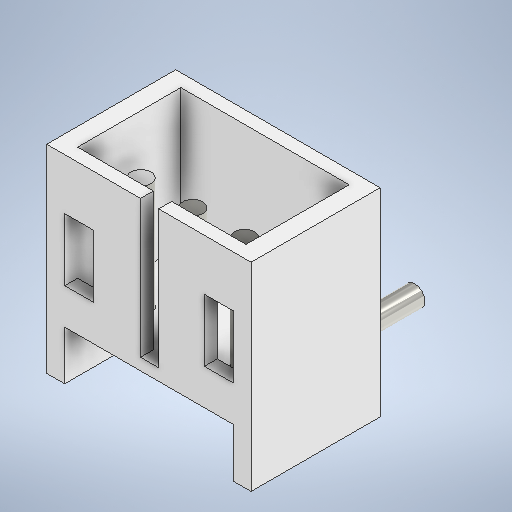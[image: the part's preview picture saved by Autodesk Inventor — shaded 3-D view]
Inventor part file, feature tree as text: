
AUTODESK INVENTOR PART (.ipt)
format: ipt  version: 2025 (Build 290162000, 162)  size: 325,632 bytes
history: native  units: in
note: dims shown in document units (in); Inventor stores cm internally (conversion verified against a paired STEP export)
features: sketch x6, extrude x4, plane x1, sweep x1
ambient origin geometry x8: Origin, YZ Plane, XZ Plane, XY Plane, X Axis, Y Axis, Z Axis, Center Point
bodies: Solid1 (feature_tree)
feature tree (12):
  extrude  "Extrusion1"  Depth=0.312in
  extrude  "Extrusion3"  Depth=0.0985in
  extrude  "Extrusion4"  Depth=0.075in TaperAngle=0.0deg
  extrude  "Extrusion7"  Depth=0.0439in
  sketch  "Sketch10"  dims[d38=1.0in d39=0.0in d40=0.067in]
  plane  "Work Plane1"
  sweep  "Sweep1"
  sketch  "Sketch1"  dims[d0=0.303in d1=0.312in]
  sketch  "Sketch4"  dims[d2=0.197in d3=0.0in d16=0.0985in]
  sketch  "Sketch5"  dims[d17=0.21in d18=0.0in d19=0.075in d20=0.0in]
  sketch  "Sketch9"  dims[d36=0.0439in d37=0.0439in]
  sketch  "Sketch11"  dims[d41=0.031in d42=0.1285in d43=0.031in d44=0.067in d45=0.079in d46=0.031in d47=0.067in d48=0.079in d49=0.0394in d50=0.13in d51=0.246in d52=0.02in d53=0.0in d54=0.0in]
